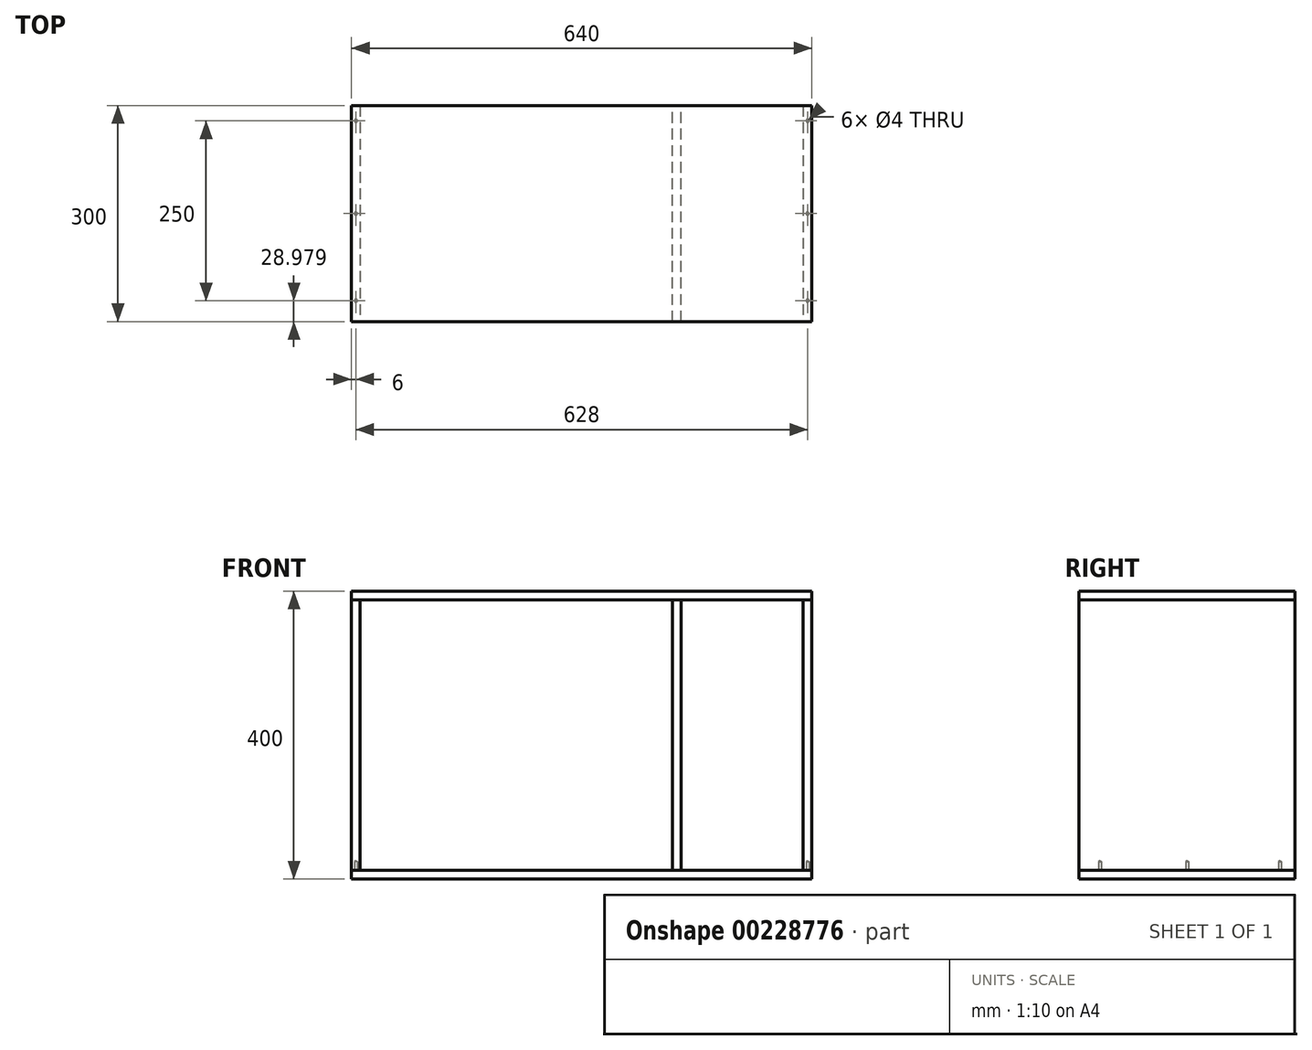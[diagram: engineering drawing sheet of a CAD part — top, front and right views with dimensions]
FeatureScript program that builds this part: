
annotation { "Feature Type Name" : "Feature", "Feature Type Description" : "" }
export const myFeature = defineFeature(function(context is Context, id is Id, definition is map)
    precondition{}
    {
        {
            var Q0;
            Q0=qCreatedBy(makeId("Top.planeOp"),FACE);
            var sketch = newSketch(context, id + "F0", { "sketchPlane" : qUnion([Q0])});
            skLineSegment(sketch, "E0.bottom", {"start": v(320, 150) * mm, "end": v(-320, 150) * mm});
            skLineSegment(sketch, "E0.top", {"start": v(320, -150) * mm, "end": v(-320, -150) * mm});
            skLineSegment(sketch, "E0.left", {"start": v(320, 150) * mm, "end": v(320, -150) * mm});
            skLineSegment(sketch, "E0.right", {"start": v(-320, 150) * mm, "end": v(-320, -150) * mm});
            skPoint(sketch, "E0.middle", {"position": v(0, 0) * mm});
            skSolve(sketch);
        }
        {
            var Q0;
            Q0=makeQuery(id+"F0.imprint","IMPRINT",FACE,{"disambiguationData":[TD([[makeQuery(id+"F0.imprint","IMPRINT",EDGE,{"derivedFrom":sQuery(id+"F0.wireOp",EDGE,"E0.bottom")}),1.0]])]});
            extrude(context, id + "F1", {"entities" : qUnion([Q0]), "depth" : 12 * mm});
        }
        {
            var Q0;
            Q0=makeQuery(id+"F1.opExtrude","SWEPT_FACE",FACE,{"disambiguationData":[OSD([sQuery(id+"F0.wireOp",EDGE,"E0.left")])]});
            var sketch = newSketch(context, id + "F2", { "sketchPlane" : qUnion([Q0])});
            skLineSegment(sketch, "E1.bottom", {"start": v(-150, 12) * mm, "end": v(150, 12) * mm});
            skLineSegment(sketch, "E1.top", {"start": v(-150, 388) * mm, "end": v(150, 388) * mm});
            skLineSegment(sketch, "E1.left", {"start": v(-150, 12) * mm, "end": v(-150, 388) * mm});
            skLineSegment(sketch, "E1.right", {"start": v(150, 12) * mm, "end": v(150, 388) * mm});
            skSolve(sketch);
        }
        {
            var Q0;
            Q0=makeQuery(id+"F2.imprint","IMPRINT",FACE,{"disambiguationData":[TD([[makeQuery(id+"F2.imprint","IMPRINT",EDGE,{"derivedFrom":sQuery(id+"F2.wireOp",EDGE,"E1.bottom")}),-1.0]])]});
            extrude(context, id + "F3", {"entities" : qUnion([Q0]), "oppositeDirection" : true, "depth" : 12 * mm});
        }
        {
            var Q0;
            Q0=makeQuery(id+"F3.opExtrude","SWEPT_FACE",FACE,{"disambiguationData":[OSD([sQuery(id+"F2.wireOp",EDGE,"E1.bottom")])]});
            var sketch = newSketch(context, id + "F4", { "sketchPlane" : qUnion([Q0])});
            skPoint(sketch, "E2", {"position": v(314, 121.02) * mm});
            skPoint(sketch, "E3", {"position": v(314, 0) * mm});
            skPoint(sketch, "E4", {"position": v(314, -128.98) * mm});
            skLineSegment(sketch, "E5", {"start": v(314, 121.02) * mm, "end": v(314, -128.98) * mm});
            skSolve(sketch);
        }
        {
            var Q0;
            Q0=sQuery(id+"F4.wireOp",VERTEX,"E2");
            var Q1;
            Q1=sQuery(id+"F4.wireOp",VERTEX,"E3");
            var Q2;
            Q2=sQuery(id+"F4.wireOp",VERTEX,"E4");
            var Q3;
            Q3=makeQuery(id+"F3.opExtrude","SWEPT_BODY",BODY,{"disambiguationData":[OSD([sQuery(id+"F2.wireOp",EDGE,"E1.bottom"),sQuery(id+"F2.wireOp",EDGE,"E1.top"),sQuery(id+"F2.wireOp",EDGE,"E1.left"),sQuery(id+"F2.wireOp",EDGE,"E1.right")])]});
            hole(context, id + "F5", {"style" : HoleStyle.SIMPLE, "endStyle" : HoleEndStyle.BLIND, "holeDiameter" : 4 * mm, "holeDepth" : 12 * mm, "locations" : qUnion([Q0, Q1, Q2]), "scope" : qUnion([Q3])});
        }
        {
            var Q0;
            Q0=makeQuery(id+"F3.opExtrude","SWEPT_FACE",FACE,{"disambiguationData":[OSD([sQuery(id+"F2.wireOp",EDGE,"E1.bottom")])]});
            var Q1;
            Q1=makeQuery(id+"F3.opExtrude","SWEPT_FACE",FACE,{"disambiguationData":[OSD([sQuery(id+"F2.wireOp",EDGE,"E1.top")])]});
            cPlane(context, id + "F6", {"entities" : qUnion([Q0, Q1]), "cplaneType" : CPlaneType.MID_PLANE, "offset" : 25 * mm, "width" : 150 * mm, "height" : 150 * mm});
        }
        {
            var Q0;
            Q0=makeQuery(id+"F3.opExtrude","SWEPT_BODY",BODY,{"disambiguationData":[OSD([sQuery(id+"F2.wireOp",EDGE,"E1.bottom"),sQuery(id+"F2.wireOp",EDGE,"E1.top"),sQuery(id+"F2.wireOp",EDGE,"E1.left"),sQuery(id+"F2.wireOp",EDGE,"E1.right")])]});
            var Q1;
            Q1=qCreatedBy(makeId("Right.planeOp"),FACE);
            mirror(context, id + "F7", {"entities" : qUnion([Q0]), "mirrorPlane" : qUnion([Q1])});
        }
        {
            var Q0;
            Q0=makeQuery(id+"F1.opExtrude","SWEPT_BODY",BODY,{"disambiguationData":[OSD([sQuery(id+"F0.wireOp",EDGE,"E0.bottom"),sQuery(id+"F0.wireOp",EDGE,"E0.top"),sQuery(id+"F0.wireOp",EDGE,"E0.left"),sQuery(id+"F0.wireOp",EDGE,"E0.right")])]});
            var Q1;
            Q1=qCreatedBy(id+"F6.planeOp",FACE);
            mirror(context, id + "F8", {"entities" : qUnion([Q0]), "mirrorPlane" : qUnion([Q1])});
        }
        {
            var Q0;
            Q0=qCreatedBy(makeId("Front.planeOp"),FACE);
            var sketch = newSketch(context, id + "F9", { "sketchPlane" : qUnion([Q0])});
            skLineSegment(sketch, "E6.bottom", {"start": v(126, 12) * mm, "end": v(138, 12) * mm});
            skLineSegment(sketch, "E6.top", {"start": v(126, 388) * mm, "end": v(138, 388) * mm});
            skLineSegment(sketch, "E6.left", {"start": v(126, 12) * mm, "end": v(126, 388) * mm});
            skLineSegment(sketch, "E6.right", {"start": v(138, 12) * mm, "end": v(138, 388) * mm});
            skSolve(sketch);
        }
        {
            var Q0;
            Q0=makeQuery(id+"F9.imprint","IMPRINT",FACE,{"disambiguationData":[TD([[makeQuery(id+"F9.imprint","IMPRINT",EDGE,{"derivedFrom":sQuery(id+"F9.wireOp",EDGE,"E6.bottom")}),1.0]])]});
            extrude(context, id + "F10", {"entities" : qUnion([Q0]), "endBound" : BoundingType.SYMMETRIC, "depth" : 300 * mm});
        }
    });
